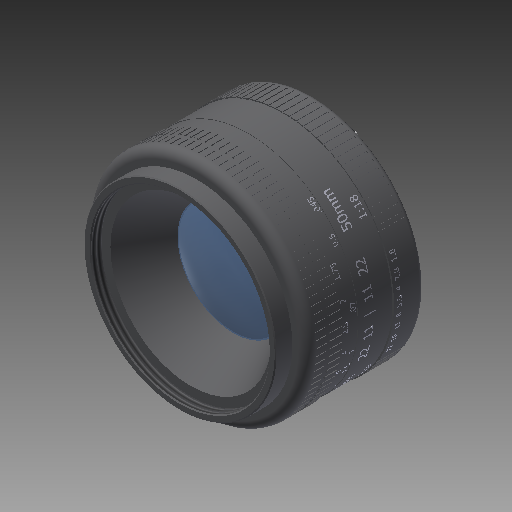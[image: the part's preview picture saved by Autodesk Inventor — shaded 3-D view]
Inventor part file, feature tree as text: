
AUTODESK INVENTOR PART (.ipt)
format: ipt  version: 2017 (Build 210142000, 142)  size: 8,681,472 bytes
history: native  units: mm (DEFAULTED — no unit token found)
features: sketch x8, revolve x4, emboss x3, extrude x2, imported_body x1, thread x1, projected_geometry x1, other x1
ambient origin geometry x8: Origin, YZ Plane, XZ Plane, XY Plane, X Axis, Y Axis, Z Axis, Center Point
bodies: Solid1 (feature_tree)
feature tree (21):
  imported_body  "Base1"
  thread  "Thread1"  [1 undecoded]
  extrude  "Extrusion1"  Depth=3.175mm
  revolve  "Revolution1"  [1 undecoded]
  emboss  "Emboss1"
  emboss  "Emboss2"
  revolve  "Revolution2"  [1 undecoded]
  revolve  "Revolution3"  [1 undecoded]
  emboss  "Emboss3"
  extrude  "Extrusion2"  TaperAngle=90.0deg  [1 undecoded]
  revolve  "Revolution4"  [1 undecoded]
  sketch  "Sketch1"  dims[d2=6.283185mm d3=3.141593mm d8=3.175mm]
  sketch  "Sketch2"  dims[d9=0.5mm d10=2.0mm d11=0.0mm]
  projected_geometry  "Projected Loop1"
  sketch  "Sketch3"  dims[d12=4.644385mm d13=0.129042mm]
  sketch  "Sketch4"  dims[d14=90.0deg d15=0.00635mm d16=0.0mm]
  sketch  "Sketch5"  dims[d17=0.00635mm d18=0.0mm d21=90.0deg]
  sketch  "Sketch6"  dims[d24=60.0deg d26=0.00381mm d27=0.0mm]
  sketch  "Sketch7"  dims[d28=10.0mm d29=0.0mm]
  other  "Open lens"
  sketch  "Sketch9"  dims[d31=90.0deg]
note: 6 required parameter values undecoded (feature->parameter linkage not recoverable at this tier; creation-order binding heuristic only, values carry confidence <= 0.55)